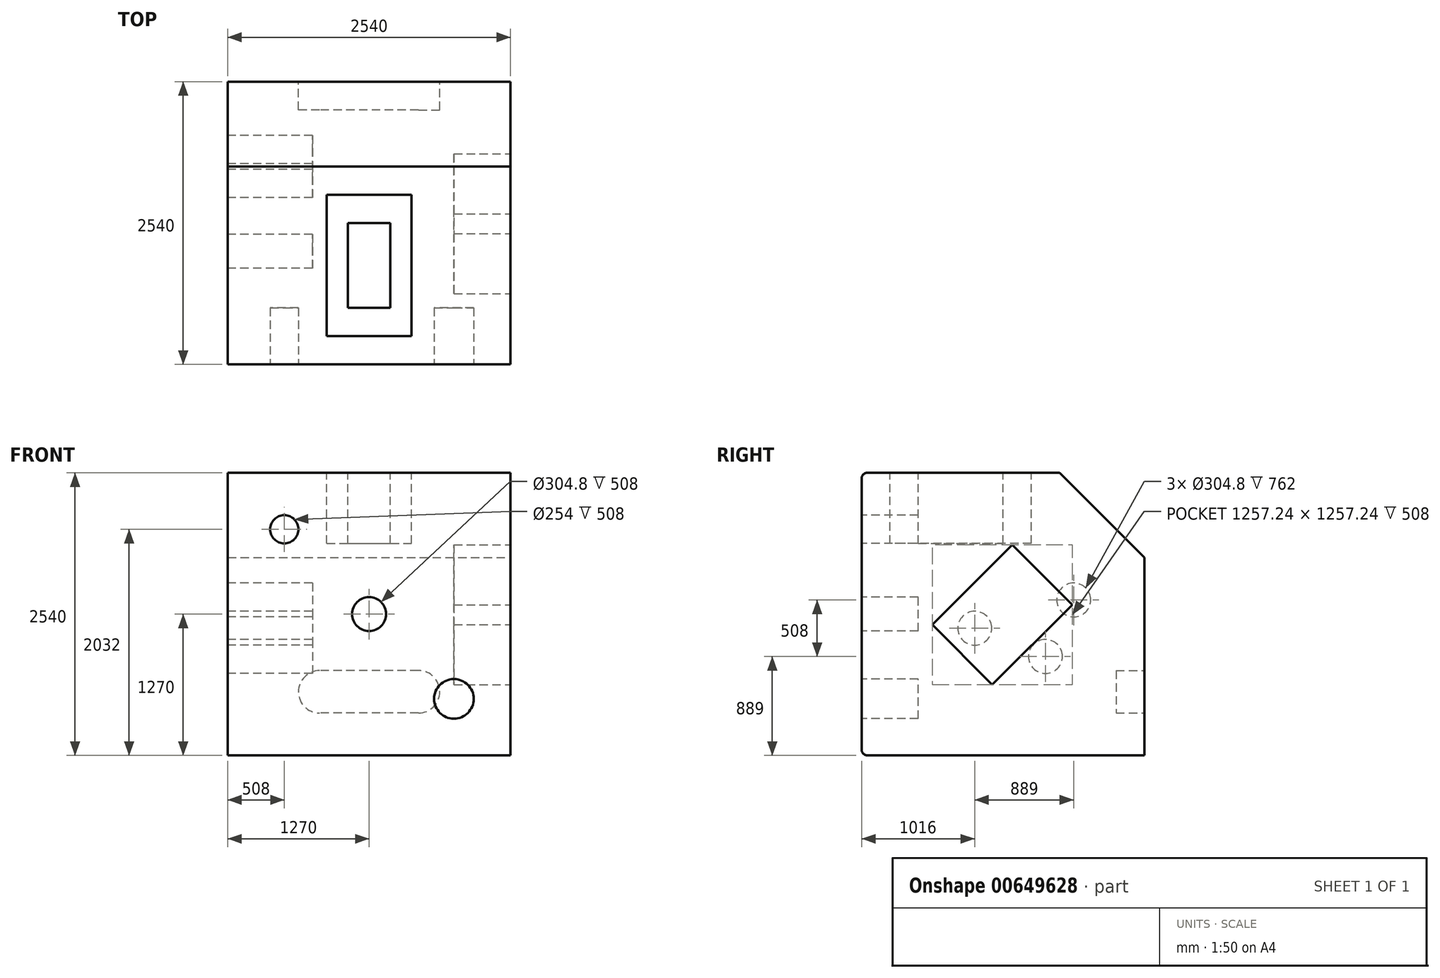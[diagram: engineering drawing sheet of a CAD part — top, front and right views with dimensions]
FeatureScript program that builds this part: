
annotation { "Feature Type Name" : "Feature", "Feature Type Description" : "" }
export const myFeature = defineFeature(function(context is Context, id is Id, definition is map)
    precondition{}
    {
        {
            var Q0;
            Q0=qCreatedBy(makeId("Front.planeOp"),FACE);
            var sketch = newSketch(context, id + "F0", { "sketchPlane" : qUnion([Q0])});
            skLineSegment(sketch, "E0", {"start": v(0, 0) * mm, "end": v(0, 2540) * mm});
            skLineSegment(sketch, "E1", {"start": v(0, 2540) * mm, "end": v(-2540, 2540) * mm});
            skLineSegment(sketch, "E2", {"start": v(-2540, 2540) * mm, "end": v(-2540, 0) * mm});
            skLineSegment(sketch, "E3", {"start": v(-2540, 0) * mm, "end": v(0, 0) * mm});
            skSolve(sketch);
        }
        {
            var Q0;
            Q0=makeQuery(id+"F0.imprint","IMPRINT",FACE,{"disambiguationData":[TD([[makeQuery(id+"F0.imprint","IMPRINT",EDGE,{"derivedFrom":sQuery(id+"F0.wireOp",EDGE,"E0")}),1.0]])]});
            extrude(context, id + "F1", {"entities" : qUnion([Q0]), "depth" : 2540 * mm, "offsetDistance" : 25.4 * mm});
        }
        {
            var Q0;
            Q0=makeQuery(id+"F1.opExtrude","CAP_EDGE",EDGE,{"disambiguationData":[OSD([sQuery(id+"F0.wireOp",EDGE,"E1")])],"isStart":true});
            chamfer(context, id + "F2", {"entities" : qUnion([Q0]), "chamferType" : ChamferType.TWO_OFFSETS, "width1" : 762 * mm, "oppositeDirection" : false, "width2" : 762 * mm, "tangentPropagation" : true});
        }
        {
            var Q0;
            Q0=makeQuery(id+"F1.opExtrude","SWEPT_FACE",FACE,{"disambiguationData":[OSD([sQuery(id+"F0.wireOp",EDGE,"E1")])]});
            var sketch = newSketch(context, id + "F3", { "sketchPlane" : qUnion([Q0])});
            skLineSegment(sketch, "E4", {"start": v(-1651, -2286) * mm, "end": v(-889, -2286) * mm});
            skLineSegment(sketch, "E5", {"start": v(-889, -2286) * mm, "end": v(-889, -1016) * mm});
            skLineSegment(sketch, "E6", {"start": v(-889, -1016) * mm, "end": v(-1651, -1016) * mm});
            skLineSegment(sketch, "E7", {"start": v(-1651, -1016) * mm, "end": v(-1651, -2286) * mm});
            skLineSegment(sketch, "E8", {"start": v(-1460.5, -2032) * mm, "end": v(-1079.5, -2032) * mm});
            skLineSegment(sketch, "E9", {"start": v(-1079.5, -2032) * mm, "end": v(-1079.5, -1270) * mm});
            skLineSegment(sketch, "E10", {"start": v(-1079.5, -1270) * mm, "end": v(-1460.5, -1270) * mm});
            skLineSegment(sketch, "E11", {"start": v(-1460.5, -2032) * mm, "end": v(-1460.5, -1270) * mm});
            skSolve(sketch);
        }
        {
            var Q0;
            Q0=makeQuery(id+"F3.imprint","IMPRINT",FACE,{"disambiguationData":[TD([[makeQuery(id+"F3.imprint","IMPRINT",EDGE,{"derivedFrom":sQuery(id+"F3.wireOp",EDGE,"E4")}),1.0]])]});
            extrude(context, id + "F4", {"entities" : qUnion([Q0]), "operationType" : NewBodyOperationType.REMOVE, "oppositeDirection" : true, "depth" : 635 * mm, "offsetDistance" : 25.4 * mm});
        }
        {
            var Q0;
            Q0=makeQuery(id+"F1.opExtrude","SWEPT_FACE",FACE,{"disambiguationData":[OSD([sQuery(id+"F0.wireOp",EDGE,"E0")])]});
            var sketch = newSketch(context, id + "F5", { "sketchPlane" : qUnion([Q0])});
            skLineSegment(sketch, "E12", {"start": v(-1186.58, 1892.24) * mm, "end": v(-647.76, 1353.42) * mm});
            skLineSegment(sketch, "E13", {"start": v(-647.76, 1353.42) * mm, "end": v(-1366.18, 635) * mm});
            skLineSegment(sketch, "E14", {"start": v(-1366.18, 635) * mm, "end": v(-1905, 1173.82) * mm});
            skLineSegment(sketch, "E15", {"start": v(-1905, 1173.82) * mm, "end": v(-1186.58, 1892.24) * mm});
            skSolve(sketch);
        }
        {
            var Q0;
            Q0=makeQuery(id+"F5.imprint","IMPRINT",FACE,{"disambiguationData":[TD([[makeQuery(id+"F5.imprint","IMPRINT",EDGE,{"derivedFrom":sQuery(id+"F5.wireOp",EDGE,"E12")}),-1.0]])]});
            extrude(context, id + "F6", {"entities" : qUnion([Q0]), "operationType" : NewBodyOperationType.REMOVE, "oppositeDirection" : true, "depth" : 508 * mm, "offsetDistance" : 25.4 * mm});
        }
        {
            var Q0;
            Q0=makeQuery(id+"F1.opExtrude","CAP_FACE",FACE,{"disambiguationData":[OSD([sQuery(id+"F0.wireOp",EDGE,"E0"),sQuery(id+"F0.wireOp",EDGE,"E1"),sQuery(id+"F0.wireOp",EDGE,"E2"),sQuery(id+"F0.wireOp",EDGE,"E3")])],"isStart":false});
            var sketch = newSketch(context, id + "F7", { "sketchPlane" : qUnion([Q0])});
            skCircle(sketch, "E16", {"center": v(-2032, 2032) * mm, "radius": 127 * mm});
            skCircle(sketch, "E17", {"center": v(-1270, 1270) * mm, "radius": 152.4 * mm});
            skCircle(sketch, "E18", {"center": v(-508, 508) * mm, "radius": 177.8 * mm});
            skSolve(sketch);
        }
        {
            var Q0;
            Q0=makeQuery(id+"F7.imprint","IMPRINT",FACE,{"disambiguationData":[TD([[makeQuery(id+"F7.imprint","IMPRINT",EDGE,{"derivedFrom":sQuery(id+"F7.wireOp",EDGE,"E16")}),1.0]])]});
            var Q1;
            Q1=makeQuery(id+"F7.imprint","IMPRINT",FACE,{"disambiguationData":[TD([[makeQuery(id+"F7.imprint","IMPRINT",EDGE,{"derivedFrom":sQuery(id+"F7.wireOp",EDGE,"E17")}),1.0]])]});
            var Q2;
            Q2=makeQuery(id+"F7.imprint","IMPRINT",FACE,{"disambiguationData":[TD([[makeQuery(id+"F7.imprint","IMPRINT",EDGE,{"derivedFrom":sQuery(id+"F7.wireOp",EDGE,"E18")}),1.0]])]});
            extrude(context, id + "F8", {"entities" : qUnion([Q0, Q1, Q2]), "operationType" : NewBodyOperationType.REMOVE, "oppositeDirection" : true, "depth" : 508 * mm, "offsetDistance" : 25.4 * mm});
        }
        {
            var Q0;
            Q0=makeQuery(id+"F1.opExtrude","SWEPT_FACE",FACE,{"disambiguationData":[OSD([sQuery(id+"F0.wireOp",EDGE,"E2")])]});
            var sketch = newSketch(context, id + "F9", { "sketchPlane" : qUnion([Q0])});
            skPoint(sketch, "E19.center", {"position": v(-2.38, 5.7) * mm});
            skCircle(sketch, "E20", {"center": v(635, 1397) * mm, "radius": 152.4 * mm});
            skCircle(sketch, "E21", {"center": v(1524, 1143) * mm, "radius": 152.4 * mm});
            skCircle(sketch, "E22", {"center": v(889, 889) * mm, "radius": 152.4 * mm});
            skSolve(sketch);
        }
        {
            var Q0;
            Q0=makeQuery(id+"F1.opExtrude","CAP_FACE",FACE,{"disambiguationData":[OSD([sQuery(id+"F0.wireOp",EDGE,"E0"),sQuery(id+"F0.wireOp",EDGE,"E1"),sQuery(id+"F0.wireOp",EDGE,"E2"),sQuery(id+"F0.wireOp",EDGE,"E3")])],"isStart":true});
            var sketch = newSketch(context, id + "F10", { "sketchPlane" : qUnion([Q0])});
            skLineSegment(sketch, "E23.bottom", {"start": v(825.5, 762) * mm, "end": v(1714.5, 762) * mm});
            skLineSegment(sketch, "E23.top", {"start": v(825.5, 381) * mm, "end": v(1714.5, 381) * mm});
            skLineSegment(sketch, "E23.left", {"start": v(635, 571.5) * mm, "end": v(635, 571.5) * mm});
            skLineSegment(sketch, "E23.right", {"start": v(1905, 571.5) * mm, "end": v(1905, 571.5) * mm});
            skPoint(sketch, "E24.visualSharp", {"position": v(635, 762) * mm});
            skArc(sketch, "E24.filletArc", {"start": v(825.5, 762) * mm, "mid": v(690.8, 706.2) * mm, "end": v(635, 571.5) * mm});
            skPoint(sketch, "E25.visualSharp", {"position": v(635, 381) * mm});
            skArc(sketch, "E25.filletArc", {"start": v(635, 571.5) * mm, "mid": v(690.8, 436.8) * mm, "end": v(825.5, 381) * mm});
            skPoint(sketch, "E26.visualSharp", {"position": v(1905, 381) * mm});
            skArc(sketch, "E26.filletArc", {"start": v(1714.5, 381) * mm, "mid": v(1849.2, 436.8) * mm, "end": v(1905, 571.5) * mm});
            skPoint(sketch, "E27.visualSharp", {"position": v(1905, 762) * mm});
            skArc(sketch, "E27.filletArc", {"start": v(1905, 571.5) * mm, "mid": v(1849.2, 706.2) * mm, "end": v(1714.5, 762) * mm});
            skSolve(sketch);
        }
        {
            var Q0;
            Q0=makeQuery(id+"F10.imprint","IMPRINT",FACE,{"disambiguationData":[TD([[makeQuery(id+"F10.imprint","IMPRINT",EDGE,{"derivedFrom":sQuery(id+"F10.wireOp",EDGE,"E23.bottom")}),-1.0]])]});
            extrude(context, id + "F11", {"entities" : qUnion([Q0]), "operationType" : NewBodyOperationType.REMOVE, "oppositeDirection" : true, "depth" : 254 * mm, "offsetDistance" : 25.4 * mm});
        }
        {
            var Q0;
            Q0=makeQuery(id+"F1.opExtrude","CAP_EDGE",EDGE,{"disambiguationData":[OSD([sQuery(id+"F0.wireOp",EDGE,"E3")])],"isStart":false});
            fillet(context, id + "F12", {"entities" : qUnion([Q0]), "radius" : 50.8 * mm, "tangentPropagation" : true, "allowEdgeOverflow" : false});
        }
        {
            var Q0;
            Q0=makeQuery(id+"F1.opExtrude","CAP_EDGE",EDGE,{"disambiguationData":[OSD([sQuery(id+"F0.wireOp",EDGE,"E1")])],"isStart":false});
            fillet(context, id + "F13", {"entities" : qUnion([Q0]), "radius" : 50.8 * mm, "tangentPropagation" : true, "allowEdgeOverflow" : false});
        }
        {
            var Q0;
            Q0=makeQuery(id+"F9.imprint","IMPRINT",FACE,{"disambiguationData":[TD([[makeQuery(id+"F9.imprint","IMPRINT",EDGE,{"derivedFrom":sQuery(id+"F9.wireOp",EDGE,"E20")}),1.0]])]});
            var Q1;
            Q1=makeQuery(id+"F9.imprint","IMPRINT",FACE,{"disambiguationData":[TD([[makeQuery(id+"F9.imprint","IMPRINT",EDGE,{"derivedFrom":sQuery(id+"F9.wireOp",EDGE,"E22")}),1.0]])]});
            var Q2;
            Q2=makeQuery(id+"F9.imprint","IMPRINT",FACE,{"disambiguationData":[TD([[makeQuery(id+"F9.imprint","IMPRINT",EDGE,{"derivedFrom":sQuery(id+"F9.wireOp",EDGE,"E21")}),1.0]])]});
            extrude(context, id + "F14", {"entities" : qUnion([Q0, Q1, Q2]), "operationType" : NewBodyOperationType.REMOVE, "oppositeDirection" : true, "depth" : 762 * mm, "offsetDistance" : 25.4 * mm});
        }
    });
